# Revit family: Fleet 3-112-xx Fan w-Lighting Fixture
name_source: partatom
category: Luminarias
units: mm (PartAtom-declared; Revit-internal decimal feet)

## family parameters
Anfitrión = Techo
Compartido = No
Corte con vacíos al cargar = No
Cota de conector redondo = Diámetro de uso
Mantener orientación de anotación = No
Origen de luz = Sí
Punto de cálculo de habitación = No
Siempre vertical = Sí
Tipo de pieza = Normal

## types (6) — shared parameters
Cambio de temperatura de color de luz atenuada = <Ninguno>
Fabricante = Oxygen - Lighting & Fans
Filtro de color = 16777215
Main Diffuser = Matte White Acrylic
Modelo = 3-112-xx/37-112-xx Fleet Fan
References = Ref. 3 = 120 V / Ref. 37 = 277 V
Tamaño de símbolo de origen de luz = 610 mm
URL = www.oxygenlighting.com
Voltage Input = 120 V or 277 V - 50/60 Hz
zero-valued in all types: Elevación por defecto

## per-type parameters (varying)
| type | Blade Finish | Metal Finish | Voltage |
| 3-112-15 / Black - Weathered Gray Blades | Weathered Gray Blades | 15 - Black | 120 V |
| 3-112-24 / Satin Nickel - Silver Blades | Silver | 24 - Satin Nickel | 120 V |
| 3-112-40 / Aged Brass - Matte Black | 15 - Black | 40 - Aged Brass | 120 V |
| 37-112-15 / Black - Weathered Gray Blades | Weathered Gray Blades | 15 - Black | 277 V |
| 37-112-24 / Satin Nickel - Silver Blades | Silver | 24 - Satin Nickel | 277 V |
| 37-112-40 / Aged Brass - Matte Black | 15 - Black | 40 - Aged Brass | 277 V |

## geometry (parser evidence)
native form markers: Blend x10, Extrusion x2, Sweep x10
no freeform markers — native parametric forms only
